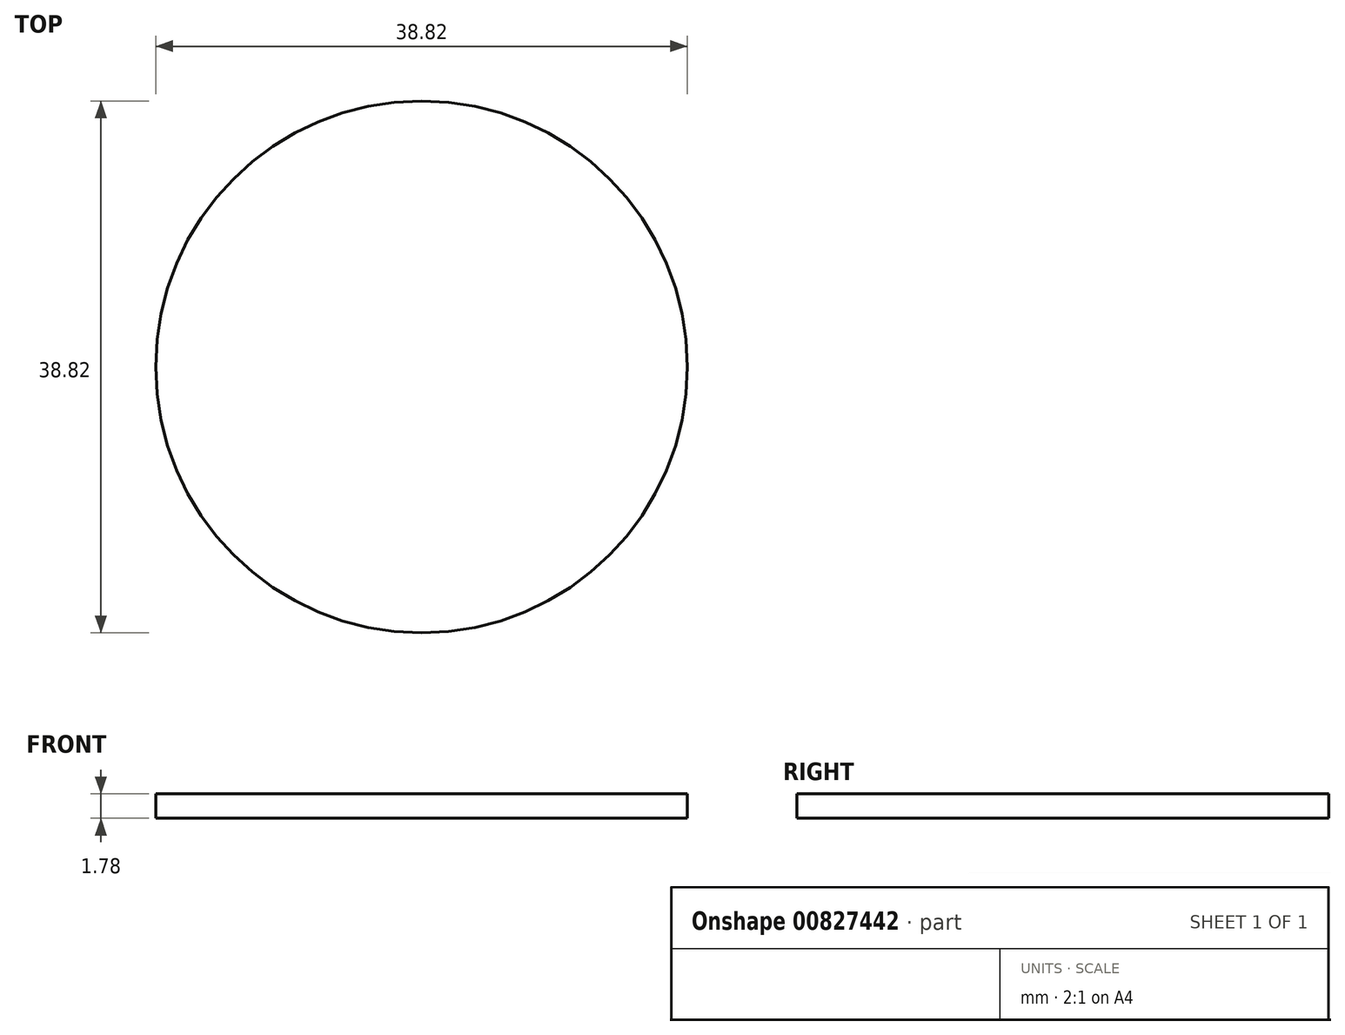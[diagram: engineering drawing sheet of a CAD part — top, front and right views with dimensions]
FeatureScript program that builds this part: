
annotation { "Feature Type Name" : "Feature", "Feature Type Description" : "" }
export const myFeature = defineFeature(function(context is Context, id is Id, definition is map)
    precondition{}
    {
        {
            var Q0;
            Q0=qCreatedBy(makeId("Top.planeOp"),FACE);
            var sketch = newSketch(context, id + "F0", { "sketchPlane" : qUnion([Q0])});
            skCircle(sketch, "E0", {"center": v(0, 0) * mm, "radius": 19.4 * mm});
            skSolve(sketch);
        }
        {
            var Q0;
            Q0 = qSketchRegion(id + "F0", true);
            extrude(context, id + "F1", {"entities" : qUnion([Q0]), "depth" : 1.78 * mm, "offsetDistance" : 25.4 * mm});
        }
    });
